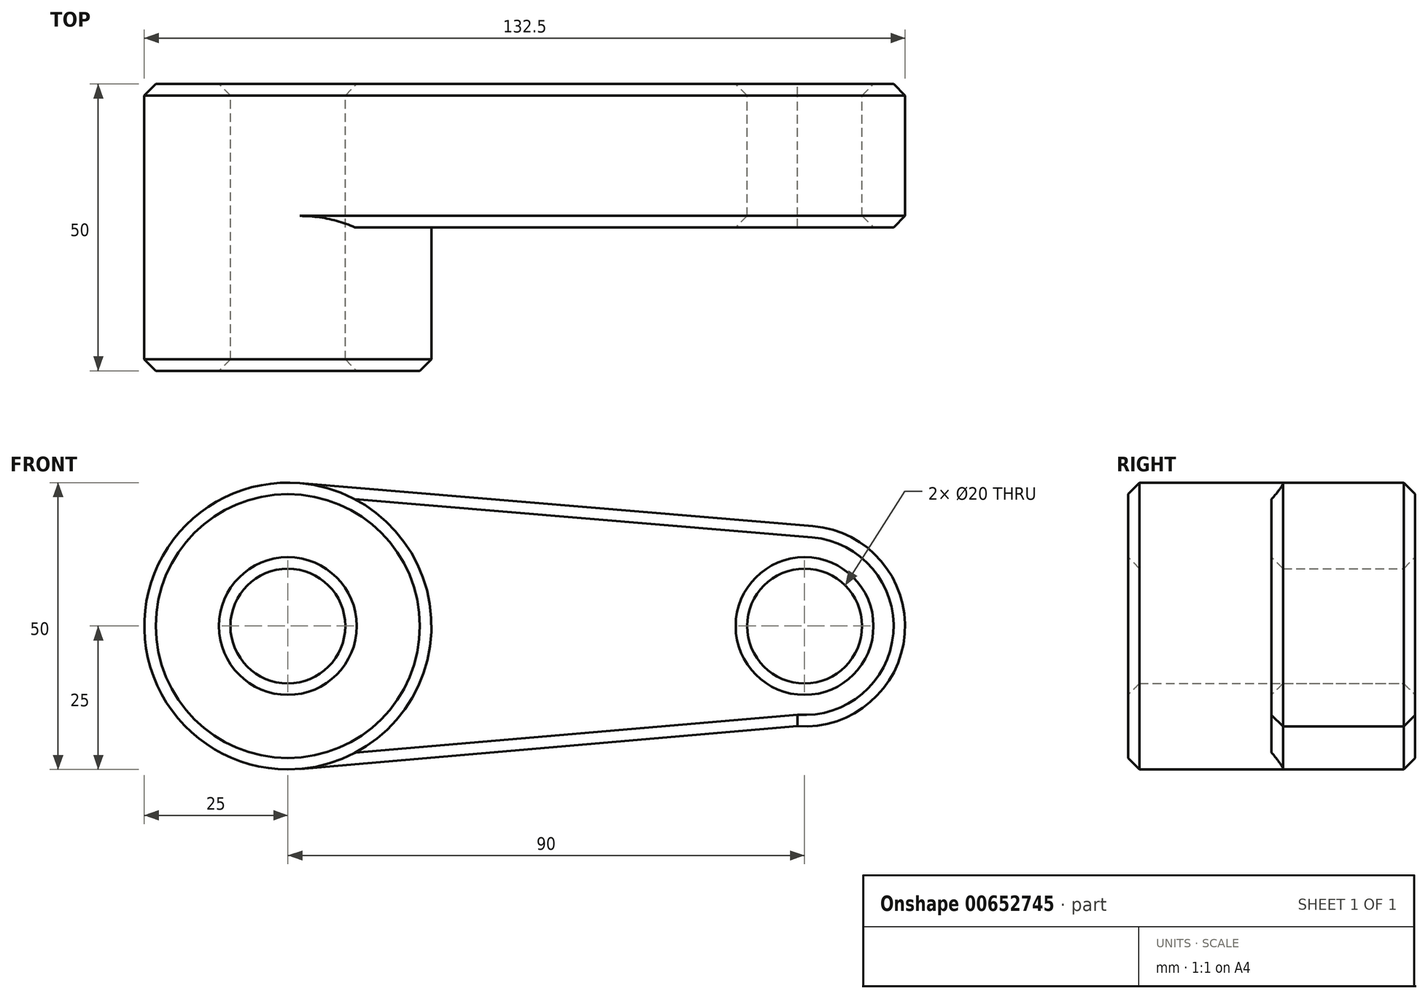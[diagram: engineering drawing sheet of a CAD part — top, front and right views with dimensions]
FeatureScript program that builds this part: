
annotation { "Feature Type Name" : "Feature", "Feature Type Description" : "" }
export const myFeature = defineFeature(function(context is Context, id is Id, definition is map)
    precondition{}
    {
        {
            var Q0;
            Q0=qCreatedBy(makeId("Front.planeOp"),FACE);
            var sketch = newSketch(context, id + "F0", { "sketchPlane" : qUnion([Q0])});
            skCircle(sketch, "E0", {"center": v(0, 0) * mm, "radius": 25 * mm});
            skCircle(sketch, "E1", {"center": v(90, 0) * mm, "radius": 17.5 * mm});
            skLineSegment(sketch, "E2", {"start": v(2.08, 24.91) * mm, "end": v(91.46, 17.44) * mm});
            skLineSegment(sketch, "E3", {"start": v(88.75, -17.46) * mm, "end": v(2.14, -24.9) * mm});
            skCircle(sketch, "E4", {"center": v(0, 0) * mm, "radius": 10 * mm});
            skCircle(sketch, "E5", {"center": v(90, 0) * mm, "radius": 10 * mm});
            skSolve(sketch);
        }
        {
            var Q0;
            Q0 = qSketchRegion(id + "F0", true);
            extrude(context, id + "F1", {"entities" : qUnion([Q0]), "depth" : 25 * mm, "offsetDistance" : 25 * mm});
        }
        {
            var Q0;
            Q0=makeQuery(id+"F0.imprint","IMPRINT",FACE,{"disambiguationData":[TD([[makeQuery(id+"F0.imprint","IMPRINT",EDGE,{"derivedFrom":sQuery(id+"F0.wireOp",EDGE,"E4")}),-1.0]])]});
            extrude(context, id + "F2", {"entities" : qUnion([Q0]), "operationType" : NewBodyOperationType.ADD, "depth" : 50 * mm, "offsetDistance" : 25 * mm});
        }
        {
            var Q0;
            Q0=makeQuery(id+"F2.opExtrude","CAP_EDGE",EDGE,{"disambiguationData":[OSD([sQuery(id+"F0.wireOp",EDGE,"E4")])],"isStart":false});
            var Q1;
            Q1=makeQuery(id+"F2.opExtrude","CAP_EDGE",EDGE,{"disambiguationData":[OSD([sQuery(id+"F0.wireOp",EDGE,"E0")])],"isStart":false});
            var Q2;
            Q2=makeQuery(id+"F1.opExtrude","CAP_EDGE",EDGE,{"disambiguationData":[OSD([sQuery(id+"F0.wireOp",EDGE,"E5")])],"isStart":false});
            chamfer(context, id + "F3", {"entities" : qUnion([Q0, Q1, Q2]), "width" : 2 * mm, "tangentPropagation" : true});
        }
        {
            var Q0;
            Q0=makeQuery(id+"F1.opExtrude","CAP_EDGE",EDGE,{"disambiguationData":[OSD([sQuery(id+"F0.wireOp",EDGE,"E3")])],"isStart":false});
            var Q1;
            Q1=makeQuery(id+"F1.opExtrude","CAP_EDGE",EDGE,{"disambiguationData":[OSD([sQuery(id+"F0.wireOp",EDGE,"E1")])],"isStart":false});
            var Q2;
            Q2=makeQuery(id+"F1.opExtrude","CAP_EDGE",EDGE,{"disambiguationData":[OSD([sQuery(id+"F0.wireOp",EDGE,"E1")])],"isStart":true});
            var Q3;
            Q3=makeQuery(id+"F1.opExtrude","CAP_EDGE",EDGE,{"disambiguationData":[OSD([sQuery(id+"F0.wireOp",EDGE,"E5")])],"isStart":true});
            var Q4;
            Q4=makeQuery(id+"F1.opExtrude","CAP_EDGE",EDGE,{"disambiguationData":[OSD([sQuery(id+"F0.wireOp",EDGE,"E4")])],"isStart":true});
            chamfer(context, id + "F4", {"entities" : qUnion([Q0, Q1, Q2, Q3, Q4]), "width" : 2 * mm, "tangentPropagation" : true});
        }
    });
